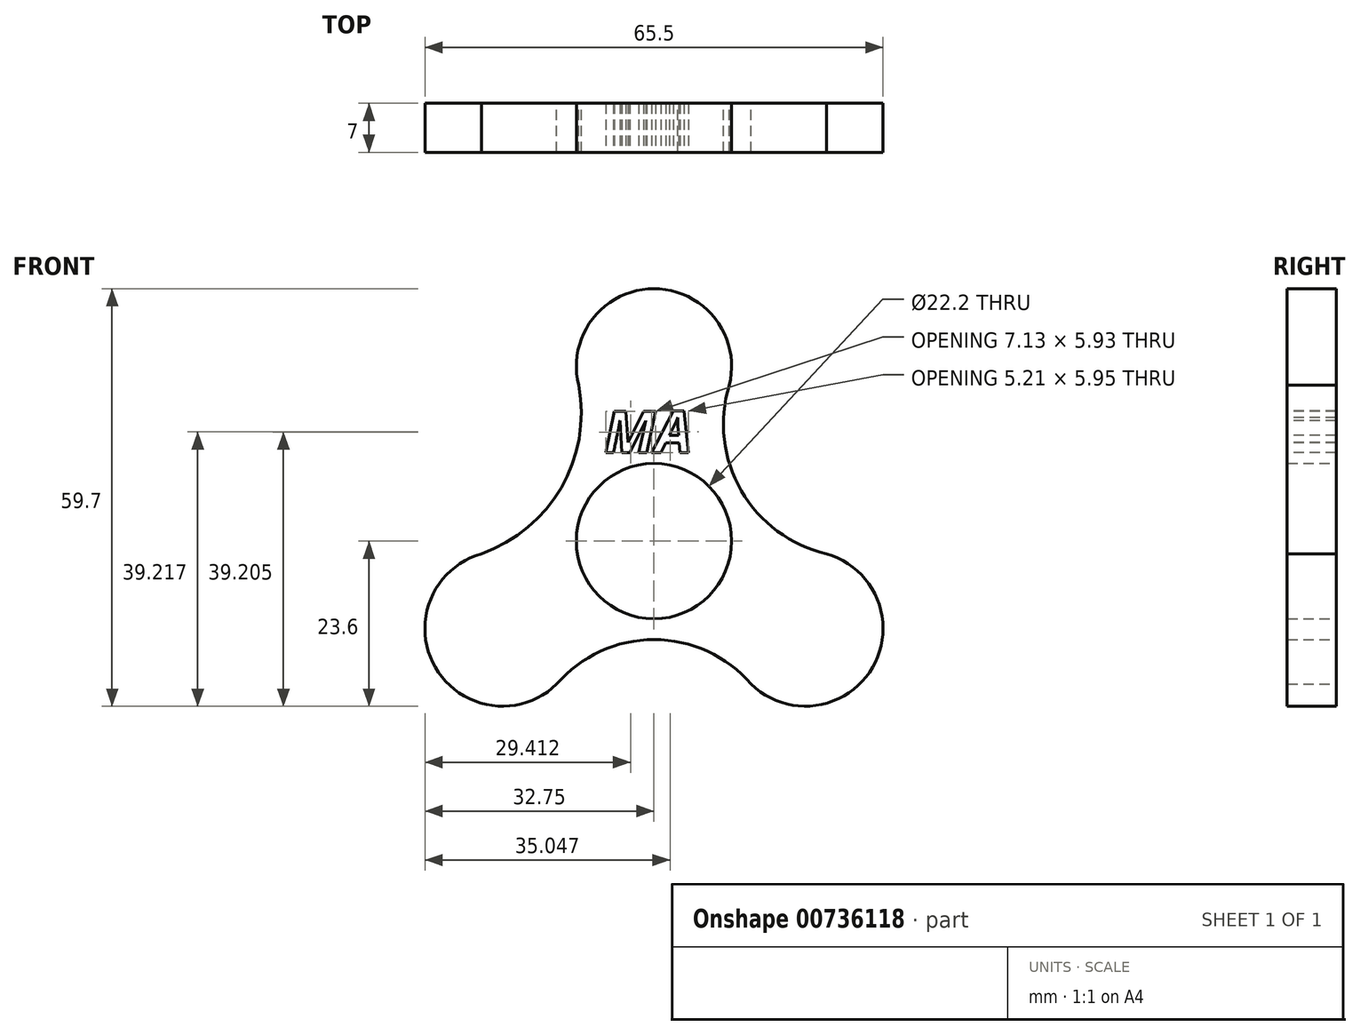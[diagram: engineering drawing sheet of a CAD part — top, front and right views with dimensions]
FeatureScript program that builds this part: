
annotation { "Feature Type Name" : "Feature", "Feature Type Description" : "" }
export const myFeature = defineFeature(function(context is Context, id is Id, definition is map)
    precondition{}
    {
        {
            var Q0;
            Q0=qCreatedBy(makeId("Front.planeOp"),FACE);
            var sketch = newSketch(context, id + "F0", { "sketchPlane" : qUnion([Q0])});
            skCircle(sketch, "E0", {"center": v(0, 0) * mm, "radius": 11.1 * mm});
            skCircle(sketch, "E1", {"center": v(0, 25) * mm, "radius": 11.1 * mm});
            skCircle(sketch, "E2.1.0", {"center": v(-21.65, -12.5) * mm, "radius": 11.1 * mm});
            skCircle(sketch, "E2.2.0", {"center": v(21.65, -12.5) * mm, "radius": 11.1 * mm});
            skArc(sketch, "E3", {"start": v(-24.67, -1.82) * mm, "mid": v(-13.26, 7.66) * mm, "end": v(-10.76, 22.27) * mm});
            skArc(sketch, "E4", {"start": v(13.91, -20.46) * mm, "mid": v(0, -14.08) * mm, "end": v(-13.91, -20.46) * mm});
            skArc(sketch, "E5", {"start": v(10.76, 22.27) * mm, "mid": v(12.48, 7.2) * mm, "end": v(24.67, -1.82) * mm});
            skSolve(sketch);
        }
        {
            var Q0;
            Q0=makeQuery(id+"F0.imprint","IMPRINT",FACE,{"disambiguationData":[TD([[makeQuery(id+"F0.imprint","IMPRINT",EDGE,{"derivedFrom":sQuery(id+"F0.wireOp",EDGE,"E0")}),-1.0]])]});
            var Q1;
            {var subQ0=sQuery(id+"F0.wireOp",EDGE,"E2.1.0");var subQ1=makeQuery(id+"F0.imprint","INTERSECT",VERTEX,{"derivedFrom":[subQ0,sQuery(id+"F0.wireOp",EDGE,"E3")]});Q1=makeQuery(id+"F0.imprint","IMPRINT",FACE,{"disambiguationData":[TD([[makeQuery(id+"F0.imprint","IMPRINT",EDGE,{"disambiguationData":[TD([[subQ1,1.0]])],"derivedFrom":subQ0}),1.0]])]});}
            var Q2;
            {var subQ0=sQuery(id+"F0.wireOp",EDGE,"E5");var subQ1=sQuery(id+"F0.wireOp",EDGE,"E2.2.0");var subQ2=makeQuery(id+"F0.imprint","INTERSECT",VERTEX,{"disambiguationData":[OD(1.0)],"derivedFrom":[subQ1,subQ0]});Q2=makeQuery(id+"F0.imprint","IMPRINT",FACE,{"disambiguationData":[TD([[makeQuery(id+"F0.imprint","IMPRINT",EDGE,{"disambiguationData":[TD([[subQ2,-1.0]])],"derivedFrom":subQ1}),1.0]])]});}
            var Q3;
            {var subQ0=sQuery(id+"F0.wireOp",EDGE,"E1");var subQ1=makeQuery(id+"F0.imprint","INTERSECT",VERTEX,{"derivedFrom":[subQ0,sQuery(id+"F0.wireOp",EDGE,"E3")]});Q3=makeQuery(id+"F0.imprint","IMPRINT",FACE,{"disambiguationData":[TD([[makeQuery(id+"F0.imprint","IMPRINT",EDGE,{"disambiguationData":[TD([[subQ1,-1.0]])],"derivedFrom":subQ0}),1.0]])]});}
            extrude(context, id + "F1", {"entities" : qUnion([Q0, Q1, Q2, Q3]), "depth" : 7 * mm, "offsetDistance" : 25 * mm});
        }
        {
            var Q0;
            Q0=makeQuery(id+"F1.opExtrude","CAP_FACE",FACE,{"disambiguationData":[OSD([sQuery(id+"F0.wireOp",EDGE,"E0"),sQuery(id+"F0.wireOp",EDGE,"E1"),sQuery(id+"F0.wireOp",EDGE,"E2.1.0"),sQuery(id+"F0.wireOp",EDGE,"E2.2.0"),sQuery(id+"F0.wireOp",EDGE,"E3"),sQuery(id+"F0.wireOp",EDGE,"E4"),sQuery(id+"F0.wireOp",EDGE,"E5")])],"isStart":false});
            var sketch = newSketch(context, id + "F2", { "sketchPlane" : qUnion([Q0])});
            skText(sketch, "E6", { "text": "MA", "fontName": "OpenSans-BoldItalic.ttf"});
            const initialGuessF2  = {"E6": [-0.00712, 0.01264, 1, 0, 0.00598]};
            skSetInitialGuess(sketch, initialGuessF2);
            skSolve(sketch);
        }
        {
            var Q0;
            Q0 = qSketchRegion(id + "F2", true);
            extrude(context, id + "F3", {"entities" : qUnion([Q0]), "operationType" : NewBodyOperationType.REMOVE, "oppositeDirection" : true, "depth" : 7 * mm, "offsetDistance" : 25 * mm});
        }
    });
